# Revit family: Medical_All_Hill-Rom_Boom-Solo-ICU
name_source: partatom
category: Specialty Equipment
revit_build: Autodesk Revit Architecture 2015 (Build: 20140606_1530(x64)
units: mm (PartAtom-declared; Revit-internal decimal feet)

## types (1)
- Boom Solo ICU 1730ML0
    Apparent Load = 0 VA
    BIMobject category = All
    BIMobject category code = medical-all
    BIMobject main category = Medical
    BIMobject main category code = medical
    Brake system = Friction,Electro-pneumatic ,Electro-magnetic
    Brand url = https://construction.hill-rom.com
    Data module reorganization = Available
    Default Elevation = 4' - 0"
    Depth extension kit2 = 3in (70 mm) available
    Description = Due to its highly flexible, modular design, the ceiling-mounted TruPort® Boom offers convenience in the OR, ICU and other departments across the hospital
    Design country = United States
    Edition number = 1
    Electric power module reorganization = Available
    Frequency = 0 Hz
    Gas module reorganization = Available
    Height = 0' - 0"
    Height adjustment = Available
    IFC Classification = Furniture
    Installation instructions = https://construction.hill-rom.com
    Length = 0' - 0"
    Load capacity = 176 lbs (80 kg
    Manufacturer = Trumpf Medical
    Manufacturer country = United States
    Manufacturer name = Hill-Rom
    Masterformat 2014 Code = 12 54 00
    Masterformat 2014 Description = Hospitality Furniture
    Material_black = Plastic-Hill-Rom-Black
    Material_blue = Plastic-Hill Rom-Blue
    Material_copper = Metal-Hill-Rom-Copper
    Material_handles = Plastic-Hill Rom-Blue
    Material_main = Plastic-Hill-Rom-White
    Material_red = Plastic-Hill-Rom-Red
    Material_white = Plastic-Hill-Rom-White
    Model = Boom Solo ICU 1730ML0
    Nominal height = 0' - 0"
    Nominal width = 0' - 0"
    Number of drawers per shelf = max.4
    OmniClass Code = 23-25 45 11 11
    OmniClass Description = Patient Beds
    Payload = Up to 750 lbs (340 kg)
    Power Connector Description no.2 = Power Connector Description no.2
    Power Connector Description no.3 = Power Connector Description no.3
    Power Connector Description no.4 = Power Connector Description no.4
    Power Connector Desription = Power Connector Description no.1
    Power Factor = 1
    Product Guid = 1cf373a3-32bd-43ae-91c0-cd05979b2bf9
    Product SKU = Trumpf-TruPort-supply-unit
    Product data url = https://bimobject.com
    Product family = Supply Units
    Product group = TruPort™
    Product url = https://www.trumpfmedical.com
    QR code = http://bimobject.com
    Support arm reach = Dual arm system: up to 102in (2600 mm)
    Technical description = https://www.trumpfmedical.com
    UNSPSC Code = 56
    URL = https://www.trumpfmedical.com
    Uniclass 1.4 Code = L8522
    Uniclass 1.4 Description = Hospital beds
    Uniclass 2015 Code = Pr_40_50_06_39
    Uniclass 2015 Name = Hospital beds
    Voltage = 120 V
    Weight Net (Kg) = 0
    Width = 0' - 0"

## geometry (parser evidence)
native form markers: Blend x6, Sweep x1
no freeform markers — native parametric forms only
